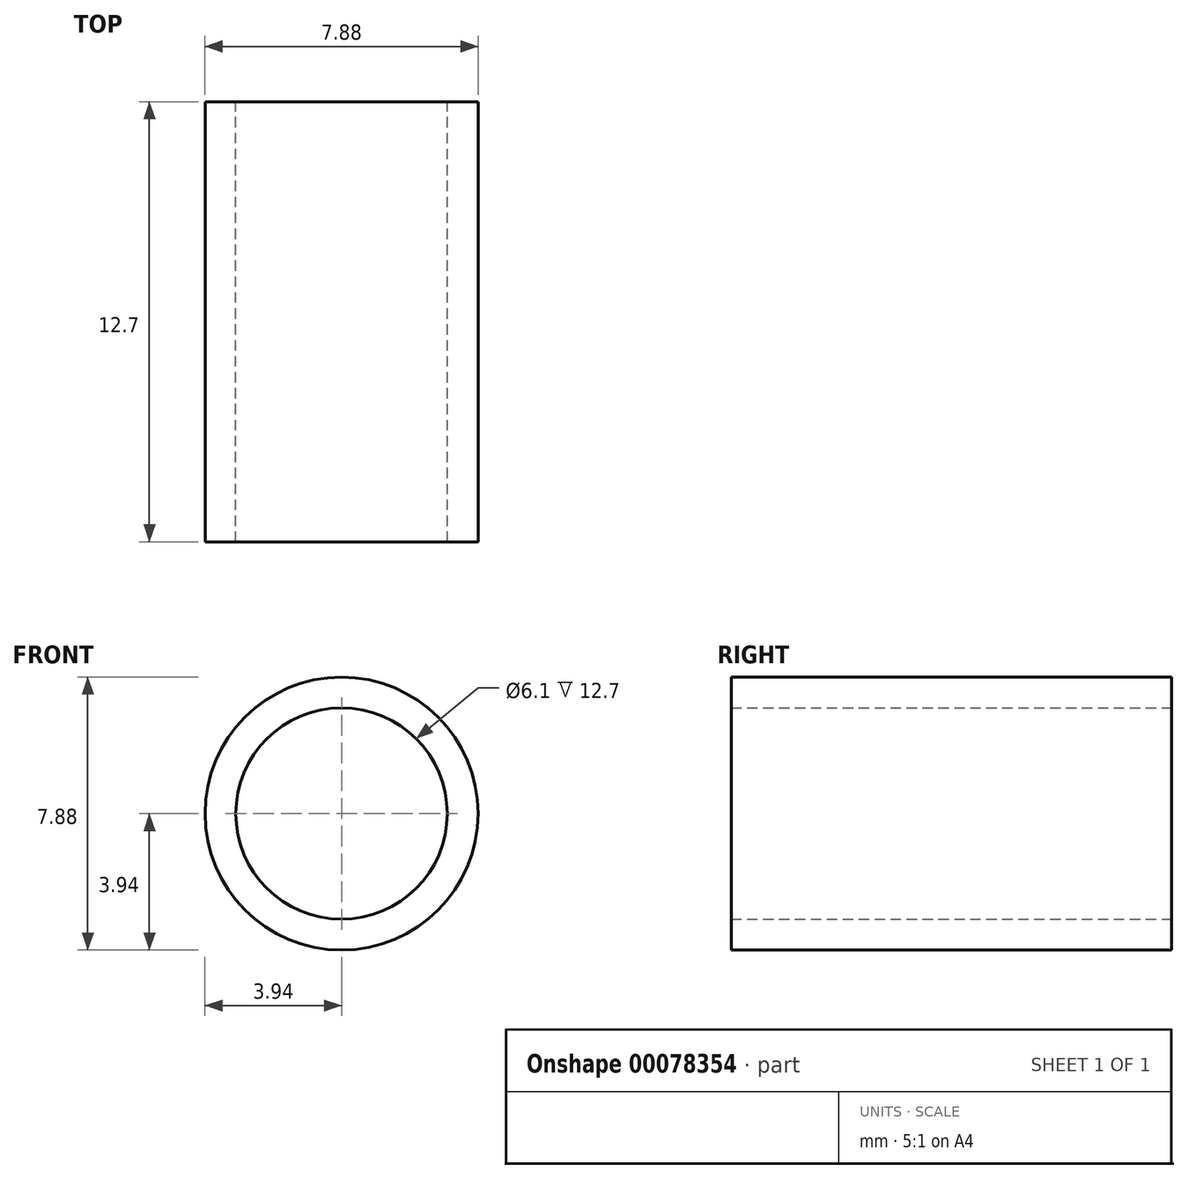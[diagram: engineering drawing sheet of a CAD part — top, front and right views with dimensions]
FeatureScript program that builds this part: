
annotation { "Feature Type Name" : "Feature", "Feature Type Description" : "" }
export const myFeature = defineFeature(function(context is Context, id is Id, definition is map)
    precondition{}
    {
        {
            var Q0;
            Q0=qCreatedBy(makeId("Front.planeOp"),FACE);
            var sketch = newSketch(context, id + "F0", { "sketchPlane" : qUnion([Q0])});
            skCircle(sketch, "E0", {"center": v(0, 0) * mm, "radius": 3.94 * mm});
            skCircle(sketch, "E1", {"center": v(0, 0) * mm, "radius": 3.05 * mm});
            skSolve(sketch);
        }
        {
            var Q0;
            Q0 = qSketchRegion(id + "F0", true);
            extrude(context, id + "F1", {"entities" : qUnion([Q0]), "endBound" : BoundingType.SYMMETRIC, "depth" : 12.7 * mm});
        }
    });
